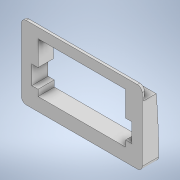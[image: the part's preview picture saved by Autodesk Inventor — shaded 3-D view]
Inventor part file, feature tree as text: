
AUTODESK INVENTOR PART (.ipt)
format: ipt  version: 2021.1 (Build 251245000, 245)  size: 1,080,832 bytes
history: native  units: in
note: dims shown in document units (in); Inventor stores cm internally (conversion verified against a paired STEP export)
features: sketch x4, extrude x3, emboss x2, plane x1, fillet x1
ambient origin geometry x8: Origin, YZ Plane, XZ Plane, XY Plane, X Axis, Y Axis, Z Axis, Center Point
bodies: Solid2 (feature_tree)
feature tree (11):
  extrude  "Extrusion3"  Depth=4.0in
  emboss  "Emboss3"
  plane  "Work Plane3"
  extrude  "Extrusion4"  Depth=22.0in
  emboss  "Emboss5"
  fillet  "Fillet1"  Radius=2.923in
  extrude  "Extrusion5"  Depth=4.82in TaperAngle=0.0deg
  sketch  "Sketch5"  dims[d5=22.0in d6=4.0in]
  sketch  "Sketch8"  dims[d7=22.0in d24=0.5in d26=2.923in]
  sketch  "Sketch9"  dims[d29=0.1in d30=4.82in d31=0.0in]
  sketch  "Sketch10"  dims[d32=0.04in d33=0.0in d36=2.0in d37=3.5in d38=0.525in d39=0.0in d40=0.0in d41=0.2in d42=0.04in d43=0.0in d44=0.1875in d45=1.375in d46=0.5in d47=0.75in d48=0.0in d49=0.0in d50=0.5in]
